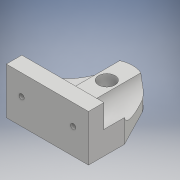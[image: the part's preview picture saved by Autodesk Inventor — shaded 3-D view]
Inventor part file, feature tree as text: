
AUTODESK INVENTOR PART (.ipt)
format: ipt  version: 2018 (Build 220112000, 112)  size: 165,376 bytes
history: native  units: mm
features: sketch x6, extrude x6
ambient origin geometry x8: Origin, YZ Plane, XZ Plane, XY Plane, X Axis, Y Axis, Z Axis, Center Point
bodies: Solid1 (feature_tree)
feature tree (12):
  sketch  "Sketch1"  dims[d9=4.5mm d10=0.0mm d11=4.5mm d12=0.0mm]
  extrude  "Extrusion1"  Depth=4.5mm TaperAngle=0.0deg
  extrude  "Extrusion2"  Depth=1.0mm
  extrude  "Extrusion3"  Depth=3.0mm
  extrude  "Extrusion4"  Depth=3.0mm
  extrude  "Extrusion5"  TaperAngle=90.0deg  [1 undecoded]
  extrude  "Extrusion6"  Depth=10.0mm
  sketch  "Sketch4"  dims[d13=1.0mm d14=1.0mm]
  sketch  "Sketch5"  dims[d15=5.5mm d16=0.0mm d17=3.0mm]
  sketch  "Sketch6"  dims[d18=3.0mm d19=11.5mm]
  sketch  "Sketch7"  dims[d23=90.0deg d24=90.0deg]
  sketch  "Sketch8"  dims[d25=10.0mm d31=5.0mm d32=120.0deg d33=14.0mm d34=6.0mm d35=6.0mm d36=10.0mm d37=0.0mm d38=5.0mm d39=5.0mm d40=5.0mm d41=5.0mm d42=10.0mm d43=0.0mm d44=10.0mm d45=0.0mm]
note: 1 required parameter value undecoded (feature->parameter linkage not recoverable at this tier; creation-order binding heuristic only, values carry confidence <= 0.55)
